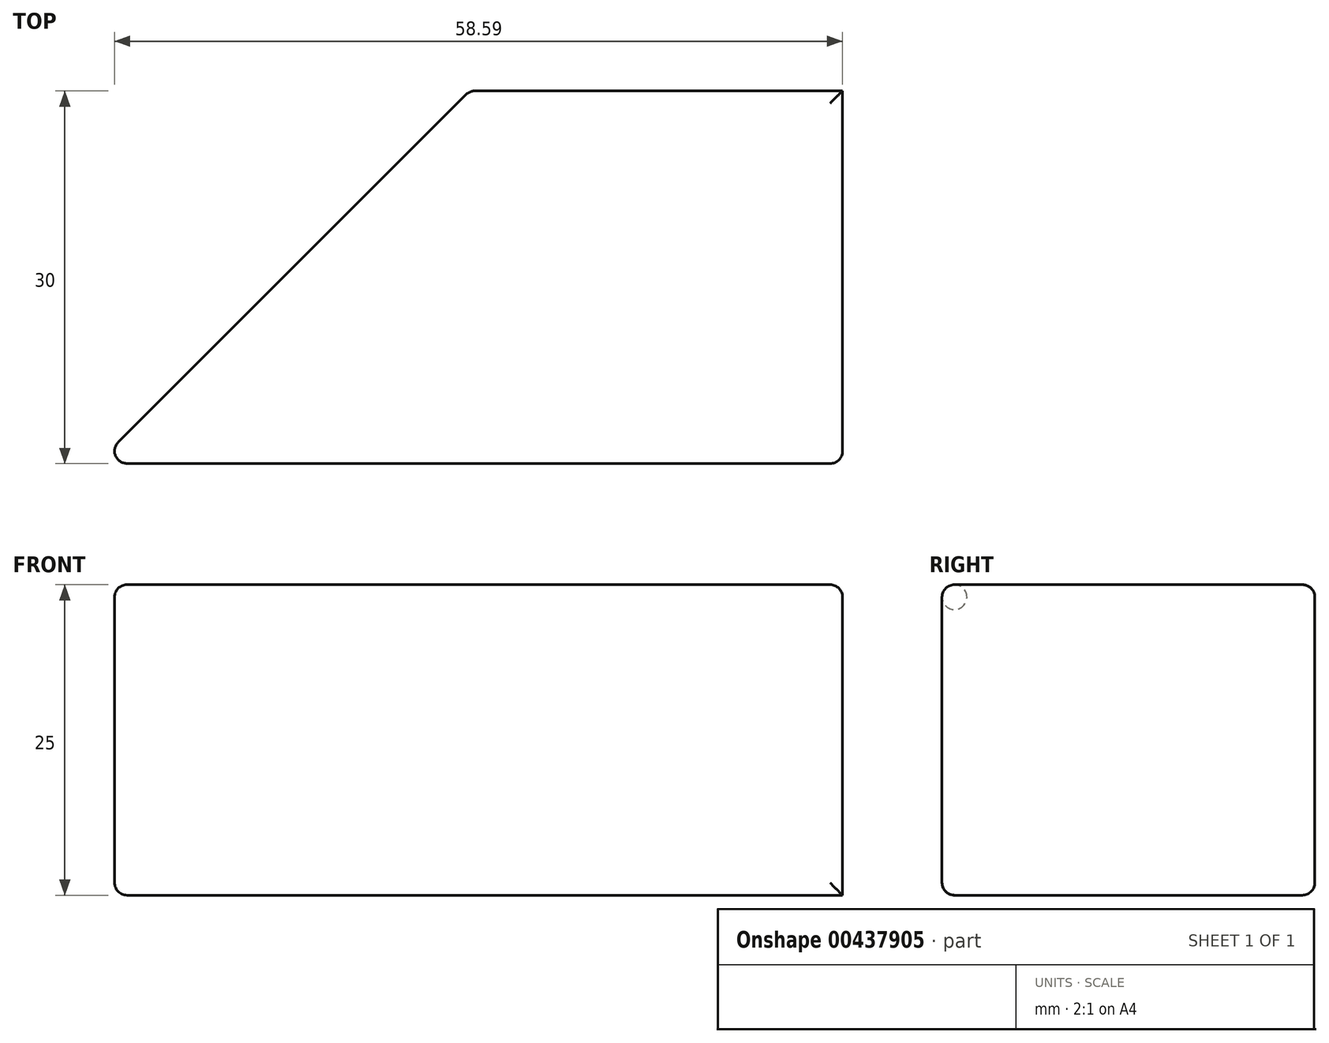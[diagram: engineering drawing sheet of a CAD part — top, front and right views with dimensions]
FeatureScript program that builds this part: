
annotation { "Feature Type Name" : "Feature", "Feature Type Description" : "" }
export const myFeature = defineFeature(function(context is Context, id is Id, definition is map)
    precondition{}
    {
        {
            var Q0;
            Q0=qCreatedBy(makeId("Top.planeOp"),FACE);
            var sketch = newSketch(context, id + "F0", { "sketchPlane" : qUnion([Q0])});
            skLineSegment(sketch, "E0.bottom", {"start": v(-24.9, 16.66) * mm, "end": v(5.1, 16.66) * mm});
            skLineSegment(sketch, "E0.top", {"start": v(-24.9, -13.34) * mm, "end": v(5.1, -13.34) * mm});
            skLineSegment(sketch, "E0.left", {"start": v(-24.9, 16.66) * mm, "end": v(-24.9, -13.34) * mm});
            skLineSegment(sketch, "E0.right", {"start": v(5.1, 16.66) * mm, "end": v(5.1, -13.34) * mm});
            skLineSegment(sketch, "E1", {"start": v(-24.9, 16.66) * mm, "end": v(-54.9, -13.33) * mm});
            skLineSegment(sketch, "E2", {"start": v(-54.9, -13.33) * mm, "end": v(-24.9, -13.34) * mm});
            skSolve(sketch);
        }
        {
            var Q0;
            Q0 = qSketchRegion(id + "F0", true);
            extrude(context, id + "F1", {"entities" : qUnion([Q0]), "depth" : 25 * mm});
        }
        {
            var Q0;
            Q0=makeQuery(id+"F1.opExtrude","CAP_EDGE",EDGE,{"disambiguationData":[OSD([sQuery(id+"F0.wireOp",EDGE,"E1")])],"isStart":false});
            var Q1;
            Q1=makeQuery(id+"F1.opExtrude","CAP_EDGE",EDGE,{"disambiguationData":[OSD([sQuery(id+"F0.wireOp",EDGE,"E2")])],"isStart":false});
            var Q2;
            Q2=makeQuery(id+"F1.opExtrude","CAP_EDGE",EDGE,{"disambiguationData":[OSD([sQuery(id+"F0.wireOp",EDGE,"E0.top")])],"isStart":false});
            var Q3;
            Q3=makeQuery(id+"F1.opExtrude","CAP_EDGE",EDGE,{"disambiguationData":[OSD([sQuery(id+"F0.wireOp",EDGE,"E0.bottom")])],"isStart":false});
            var Q4;
            Q4=makeQuery(id+"F1.opExtrude","CAP_EDGE",EDGE,{"disambiguationData":[OSD([sQuery(id+"F0.wireOp",EDGE,"E0.right")])],"isStart":false});
            var Q5;
            Q5=makeQuery(id+"F1.opExtrude","SWEPT_EDGE",EDGE,{"disambiguationData":[OSD([sQuery(id+"F0.wireOp",EDGE,"E1"),sQuery(id+"F0.wireOp",EDGE,"E2")])]});
            var Q6;
            Q6=makeQuery(id+"F1.opExtrude","CAP_EDGE",EDGE,{"disambiguationData":[OSD([sQuery(id+"F0.wireOp",EDGE,"E2")])],"isStart":true});
            var Q7;
            Q7=makeQuery(id+"F1.opExtrude","CAP_EDGE",EDGE,{"disambiguationData":[OSD([sQuery(id+"F0.wireOp",EDGE,"E0.top")])],"isStart":true});
            var Q8;
            Q8=makeQuery(id+"F1.opExtrude","SWEPT_EDGE",EDGE,{"disambiguationData":[OSD([sQuery(id+"F0.wireOp",EDGE,"E0.top"),sQuery(id+"F0.wireOp",EDGE,"E0.right")])]});
            var Q9;
            Q9=makeQuery(id+"F1.opExtrude","SWEPT_EDGE",EDGE,{"disambiguationData":[OSD([sQuery(id+"F0.wireOp",EDGE,"E0.top"),sQuery(id+"F0.wireOp",EDGE,"E0.left"),sQuery(id+"F0.wireOp",EDGE,"E2")])]});
            var Q10;
            Q10=makeQuery(id+"F1.opExtrude","CAP_EDGE",EDGE,{"disambiguationData":[OSD([sQuery(id+"F0.wireOp",EDGE,"E1")])],"isStart":true});
            var Q11;
            Q11=makeQuery(id+"F1.opExtrude","SWEPT_EDGE",EDGE,{"disambiguationData":[OSD([sQuery(id+"F0.wireOp",EDGE,"E0.bottom"),sQuery(id+"F0.wireOp",EDGE,"E0.left"),sQuery(id+"F0.wireOp",EDGE,"E1")])]});
            var Q12;
            Q12=makeQuery(id+"F1.opExtrude","CAP_EDGE",EDGE,{"disambiguationData":[OSD([sQuery(id+"F0.wireOp",EDGE,"E0.bottom")])],"isStart":true});
            fillet(context, id + "F2", {"entities" : qUnion([Q0, Q1, Q2, Q3, Q4, Q5, Q6, Q7, Q8, Q9, Q10, Q11, Q12]), "radius" : 1 * mm, "tangentPropagation" : true, "allowEdgeOverflow" : false});
        }
    });
